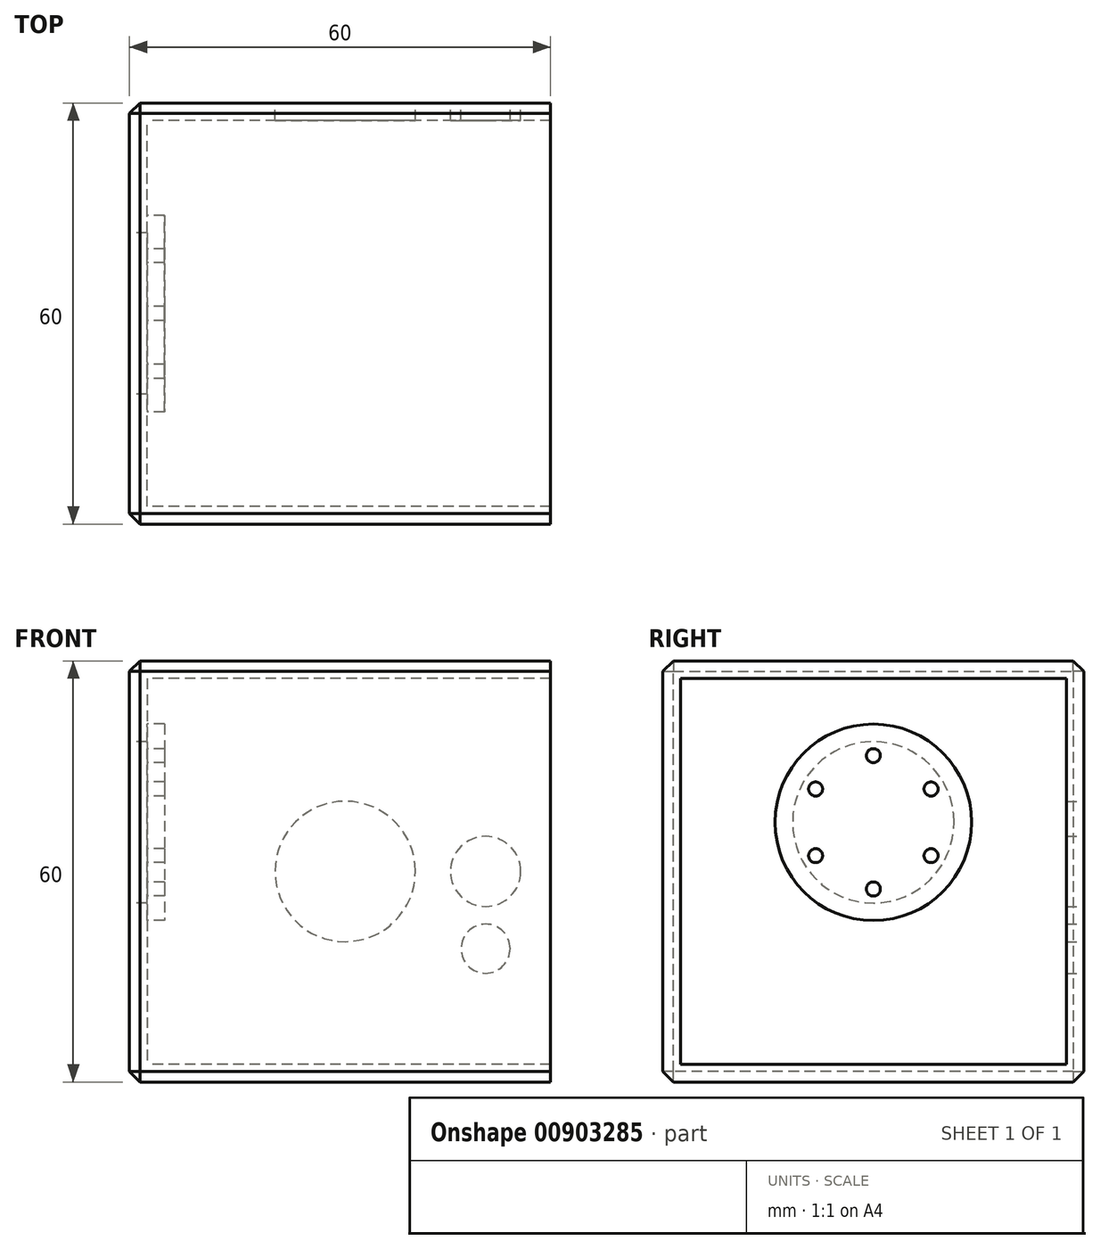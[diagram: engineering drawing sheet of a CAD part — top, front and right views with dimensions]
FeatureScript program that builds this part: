
annotation { "Feature Type Name" : "Feature", "Feature Type Description" : "" }
export const myFeature = defineFeature(function(context is Context, id is Id, definition is map)
    precondition{}
    {
        {
            var Q0;
            Q0=qCreatedBy(makeId("Right.planeOp"),FACE);
            var sketch = newSketch(context, id + "F0", { "sketchPlane" : qUnion([Q0])});
            skLineSegment(sketch, "E0.bottom", {"start": v(-30, 63) * mm, "end": v(30, 63) * mm});
            skLineSegment(sketch, "E0.top", {"start": v(-30, 3) * mm, "end": v(0, 3) * mm});
            skLineSegment(sketch, "E0.left", {"start": v(-30, 63) * mm, "end": v(-30, 3) * mm});
            skLineSegment(sketch, "E0.right", {"start": v(30, 63) * mm, "end": v(30, 3) * mm});
            skLineSegment(sketch, "E1", {"start": v(0, 0) * mm, "end": v(0, 3) * mm, "construction": true});
            skLineSegment(sketch, "E2", {"start": v(0, 3) * mm, "end": v(30, 3) * mm});
            skSolve(sketch);
        }
        {
            var Q0;
            Q0=makeQuery(id+"F0.imprint","IMPRINT",FACE,{"disambiguationData":[TD([[makeQuery(id+"F0.imprint","IMPRINT",EDGE,{"derivedFrom":sQuery(id+"F0.wireOp",EDGE,"E0.bottom")}),-1.0]])]});
            extrude(context, id + "F1", {"entities" : qUnion([Q0]), "depth" : 60 * mm, "offsetDistance" : 25 * mm});
        }
        {
            var Q0;
            Q0=makeQuery(id+"F1.opExtrude","CAP_FACE",FACE,{"disambiguationData":[OSD([sQuery(id+"F0.wireOp",EDGE,"E0.bottom"),sQuery(id+"F0.wireOp",EDGE,"E0.top"),sQuery(id+"F0.wireOp",EDGE,"E0.left"),sQuery(id+"F0.wireOp",EDGE,"E0.right"),sQuery(id+"F0.wireOp",EDGE,"E2")])],"isStart":true});
            var sketch = newSketch(context, id + "F2", { "sketchPlane" : qUnion([Q0])});
            skCircle(sketch, "E3", {"center": v(0, 40) * mm, "radius": 11.5 * mm});
            skSolve(sketch);
        }
        {
            var Q0;
            Q0=makeQuery(id+"F2.imprint","IMPRINT",FACE,{"disambiguationData":[TD([[makeQuery(id+"F2.imprint","IMPRINT",EDGE,{"derivedFrom":sQuery(id+"F2.wireOp",EDGE,"E3")}),1.0]])]});
            extrude(context, id + "F3", {"entities" : qUnion([Q0]), "operationType" : NewBodyOperationType.REMOVE, "oppositeDirection" : true, "depth" : 2.5 * mm, "offsetDistance" : 25 * mm});
        }
        {
            var Q0;
            Q0=makeQuery(id+"F1.opExtrude","CAP_FACE",FACE,{"disambiguationData":[OSD([sQuery(id+"F0.wireOp",EDGE,"E0.bottom"),sQuery(id+"F0.wireOp",EDGE,"E0.top"),sQuery(id+"F0.wireOp",EDGE,"E0.left"),sQuery(id+"F0.wireOp",EDGE,"E0.right"),sQuery(id+"F0.wireOp",EDGE,"E2")])],"isStart":true});
            var sketch = newSketch(context, id + "F4", { "sketchPlane" : qUnion([Q0])});
            skCircle(sketch, "E4", {"center": v(0, 40) * mm, "radius": 9.5 * mm, "construction": true});
            skLineSegment(sketch, "E5", {"start": v(0, 40) * mm, "end": v(0, 49.5) * mm, "construction": true});
            skCircle(sketch, "E6", {"center": v(0, 49.5) * mm, "radius": 1 * mm});
            skCircle(sketch, "E7.1.0", {"center": v(-8.23, 44.75) * mm, "radius": 1 * mm});
            skCircle(sketch, "E7.2.0", {"center": v(-8.23, 35.25) * mm, "radius": 1 * mm});
            skCircle(sketch, "E7.3.0", {"center": v(0, 30.5) * mm, "radius": 1 * mm});
            skCircle(sketch, "E7.4.0", {"center": v(8.23, 35.25) * mm, "radius": 1 * mm});
            skCircle(sketch, "E7.5.0", {"center": v(8.23, 44.75) * mm, "radius": 1 * mm});
            skSolve(sketch);
        }
        {
            var Q0;
            Q0=makeQuery(id+"F1.opExtrude","CAP_FACE",FACE,{"disambiguationData":[OSD([sQuery(id+"F0.wireOp",EDGE,"E0.bottom"),sQuery(id+"F0.wireOp",EDGE,"E0.top"),sQuery(id+"F0.wireOp",EDGE,"E0.left"),sQuery(id+"F0.wireOp",EDGE,"E0.right"),sQuery(id+"F0.wireOp",EDGE,"E2")])],"isStart":false});
            shell(context, id + "F5", {"entities" : qUnion([Q0]), "thickness" : 2.5 * mm});
        }
        {
            var Q0;
            Q0 = qSketchRegion(id + "F4", true);
            extrude(context, id + "F6", {"entities" : qUnion([Q0]), "operationType" : NewBodyOperationType.REMOVE, "oppositeDirection" : true, "depth" : 25 * mm, "offsetDistance" : 25 * mm});
        }
        {
            var Q0;
            Q0=makeQuery(id+"F1.opExtrude","SWEPT_EDGE",EDGE,{"disambiguationData":[OSD([sQuery(id+"F0.wireOp",EDGE,"E0.bottom"),sQuery(id+"F0.wireOp",EDGE,"E0.left")])]});
            var Q1;
            Q1=makeQuery(id+"F1.opExtrude","SWEPT_EDGE",EDGE,{"disambiguationData":[OSD([sQuery(id+"F0.wireOp",EDGE,"E0.bottom"),sQuery(id+"F0.wireOp",EDGE,"E0.right")])]});
            var Q2;
            Q2=makeQuery(id+"F1.opExtrude","SWEPT_EDGE",EDGE,{"disambiguationData":[OSD([sQuery(id+"F0.wireOp",EDGE,"E0.right"),sQuery(id+"F0.wireOp",EDGE,"E2")])]});
            var Q3;
            Q3=makeQuery(id+"F1.opExtrude","SWEPT_EDGE",EDGE,{"disambiguationData":[OSD([sQuery(id+"F0.wireOp",EDGE,"E0.top"),sQuery(id+"F0.wireOp",EDGE,"E0.left")])]});
            var Q4;
            Q4=makeQuery(id+"F1.opExtrude","CAP_EDGE",EDGE,{"disambiguationData":[OSD([sQuery(id+"F0.wireOp",EDGE,"E0.left")])],"isStart":true});
            var Q5;
            Q5=makeQuery(id+"F1.opExtrude","CAP_EDGE",EDGE,{"disambiguationData":[OSD([sQuery(id+"F0.wireOp",EDGE,"E0.bottom")])],"isStart":true});
            var Q6;
            Q6=makeQuery(id+"F1.opExtrude","CAP_EDGE",EDGE,{"disambiguationData":[OSD([sQuery(id+"F0.wireOp",EDGE,"E0.right")])],"isStart":true});
            var Q7;
            Q7=makeQuery(id+"F1.opExtrude","CAP_EDGE",EDGE,{"disambiguationData":[OSD([sQuery(id+"F0.wireOp",EDGE,"E0.top"),sQuery(id+"F0.wireOp",EDGE,"E2")])],"isStart":true});
            chamfer(context, id + "F7", {"entities" : qUnion([Q0, Q1, Q2, Q3, Q4, Q5, Q6, Q7]), "width" : 1.5 * mm, "tangentPropagation" : true});
        }
        {
            var Q0;
            Q0=makeQuery(id+"F1.opExtrude","SWEPT_FACE",FACE,{"disambiguationData":[OSD([sQuery(id+"F0.wireOp",EDGE,"E0.right")])]});
            var sketch = newSketch(context, id + "F8", { "sketchPlane" : qUnion([Q0])});
            skLineSegment(sketch, "E8", {"start": v(0, 0) * mm, "end": v(0, 33) * mm, "construction": true});
            skLineSegment(sketch, "E9", {"start": v(0, 33) * mm, "end": v(-30.75, 33) * mm, "construction": true});
            skLineSegment(sketch, "E10", {"start": v(-30.75, 33) * mm, "end": v(-30.75, 4.5) * mm, "construction": true});
            skLineSegment(sketch, "E11", {"start": v(-30.75, 4.5) * mm, "end": v(-30.75, 33) * mm, "construction": true});
            skLineSegment(sketch, "E12", {"start": v(-60, 33) * mm, "end": v(-30.75, 33) * mm, "construction": true});
            skCircle(sketch, "E13", {"center": v(-30.75, 33) * mm, "radius": 10 * mm});
            skCircle(sketch, "E14", {"center": v(-50.75, 33) * mm, "radius": 5 * mm});
            skCircle(sketch, "E15", {"center": v(-50.75, 22) * mm, "radius": 3.5 * mm});
            skLineSegment(sketch, "E16", {"start": v(-50.75, 33) * mm, "end": v(-50.75, 22) * mm, "construction": true});
            skLineSegment(sketch, "E17", {"start": v(-50.75, 33) * mm, "end": v(-30.75, 33) * mm, "construction": true});
            skSolve(sketch);
        }
        {
            var Q0;
            Q0=makeQuery(id+"F8.imprint","IMPRINT",FACE,{"disambiguationData":[TD([[makeQuery(id+"F8.imprint","IMPRINT",EDGE,{"derivedFrom":sQuery(id+"F8.wireOp",EDGE,"E15")}),1.0]])]});
            var Q1;
            Q1=makeQuery(id+"F8.imprint","IMPRINT",FACE,{"disambiguationData":[TD([[makeQuery(id+"F8.imprint","IMPRINT",EDGE,{"derivedFrom":sQuery(id+"F8.wireOp",EDGE,"E14")}),1.0]])]});
            var Q2;
            Q2=makeQuery(id+"F8.imprint","IMPRINT",FACE,{"disambiguationData":[TD([[makeQuery(id+"F8.imprint","IMPRINT",EDGE,{"derivedFrom":sQuery(id+"F8.wireOp",EDGE,"E13")}),1.0]])]});
            var Q3;
            Q3=sQuery(id+"F8.wireOp",EDGE,"E13");
            var Q4;
            Q4=sQuery(id+"F8.wireOp",EDGE,"E14");
            var Q5;
            Q5=sQuery(id+"F8.wireOp",EDGE,"E15");
            extrude(context, id + "F9", {"entities" : qUnion([Q0, Q1, Q2]), "operationType" : NewBodyOperationType.REMOVE, "surfaceEntities" : qUnion([Q3, Q4, Q5]), "oppositeDirection" : true, "depth" : 3 * mm, "offsetDistance" : 25 * mm});
        }
    });
